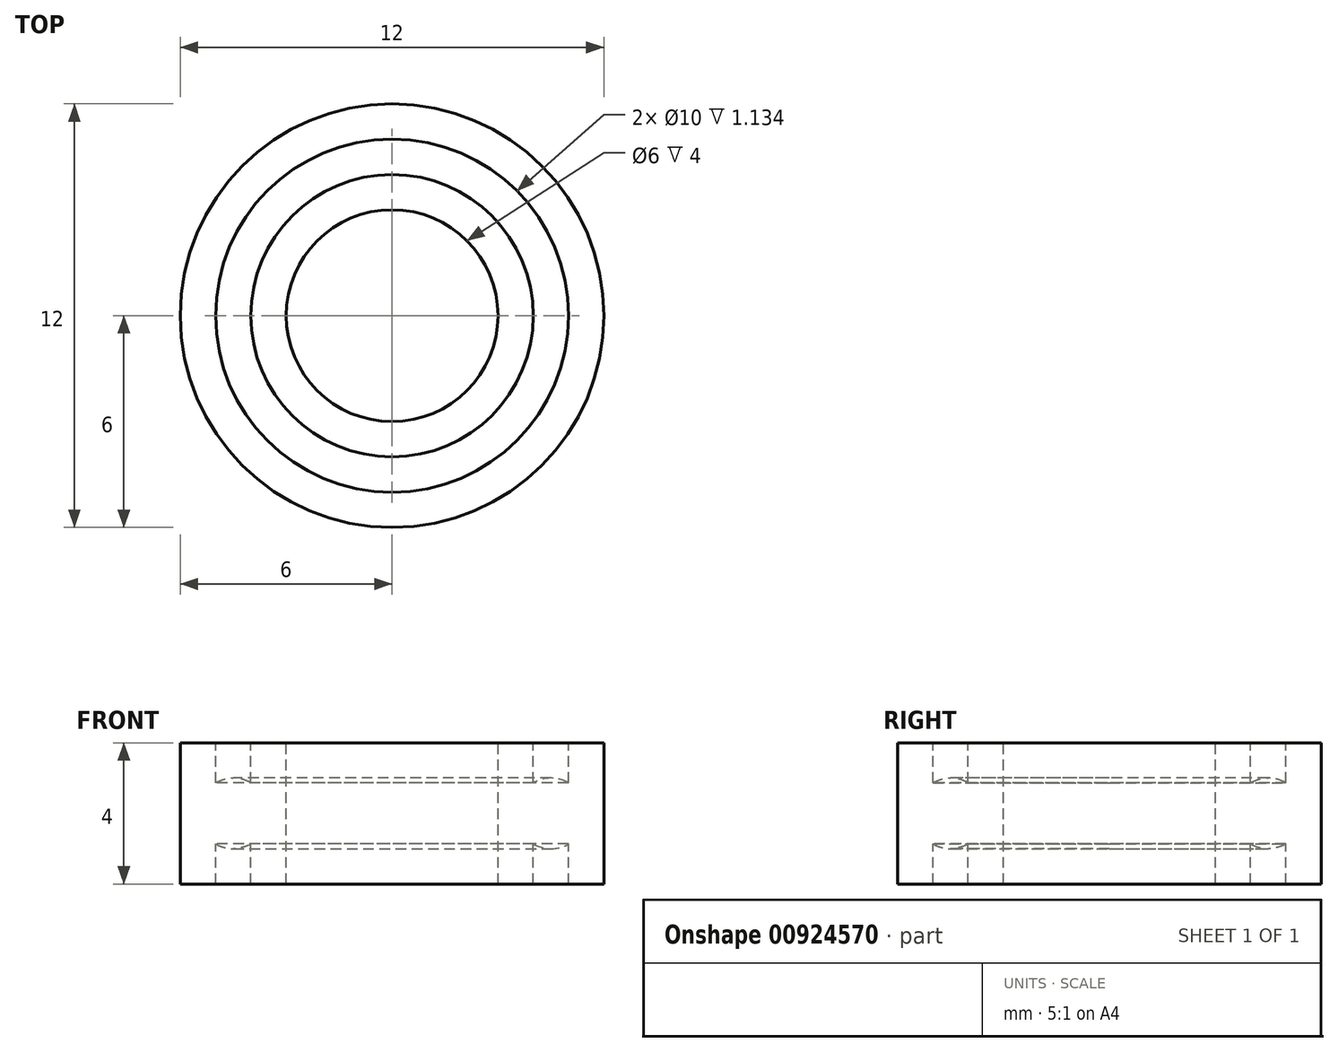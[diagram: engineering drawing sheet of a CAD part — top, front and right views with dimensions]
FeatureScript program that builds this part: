
annotation { "Feature Type Name" : "Feature", "Feature Type Description" : "" }
export const myFeature = defineFeature(function(context is Context, id is Id, definition is map)
    precondition{}
    {
        {
            var Q0;
            Q0=qCreatedBy(makeId("Front.planeOp"),FACE);
            var sketch = newSketch(context, id + "F0", { "sketchPlane" : qUnion([Q0])});
            skLineSegment(sketch, "E0", {"start": v(0, 11.53) * mm, "end": v(0, -10.93) * mm, "construction": true});
            skLineSegment(sketch, "E1.bottom", {"start": v(-3, -2) * mm, "end": v(-4, -2) * mm});
            skLineSegment(sketch, "E1.top", {"start": v(-3, 2) * mm, "end": v(-4, 2) * mm});
            skLineSegment(sketch, "E1.left", {"start": v(-3, -2) * mm, "end": v(-3, 2) * mm});
            skLineSegment(sketch, "E1.right", {"start": v(-6, -2) * mm, "end": v(-6, 2) * mm});
            skPoint(sketch, "E1.middle", {"position": v(-4.5, 0) * mm});
            skArc(sketch, "E2", {"start": v(-5, -0.87) * mm, "mid": v(-4.5, -1) * mm, "end": v(-4, -0.87) * mm});
            skLineSegment(sketch, "E3", {"start": v(-4, 2) * mm, "end": v(-4, 0.87) * mm});
            skLineSegment(sketch, "E4", {"start": v(-5, 2) * mm, "end": v(-5, 0.87) * mm});
            skArc(sketch, "E5.trimOffspring", {"start": v(-4, 0.87) * mm, "mid": v(-4.5, 1) * mm, "end": v(-5, 0.87) * mm});
            skLineSegment(sketch, "E6.trimOffspring", {"start": v(-5, 2) * mm, "end": v(-6, 2) * mm});
            skLineSegment(sketch, "E7.trimOffspring", {"start": v(-5, -2) * mm, "end": v(-6, -2) * mm});
            skLineSegment(sketch, "E8.trimOffspring", {"start": v(-5, -0.87) * mm, "end": v(-5, -2) * mm});
            skLineSegment(sketch, "E9.trimOffspring", {"start": v(-4, -0.87) * mm, "end": v(-4, -2) * mm});
            skSolve(sketch);
        }
        {
            var Q0;
            Q0=makeQuery(id+"F0.imprint","IMPRINT",FACE,{"disambiguationData":[TD([[makeQuery(id+"F0.imprint","IMPRINT",EDGE,{"derivedFrom":sQuery(id+"F0.wireOp",EDGE,"E1.bottom")}),-1.0]])]});
            var Q1;
            Q1=sQuery(id+"F0.wireOp",EDGE,"E0");
            revolve(context, id + "F1", {"surfaceOperationType" : NewSurfaceOperationType.NEW, "entities" : qUnion([Q0]), "axis" : qUnion([Q1]), "revolveType" : RevolveType.FULL});
        }
    });
